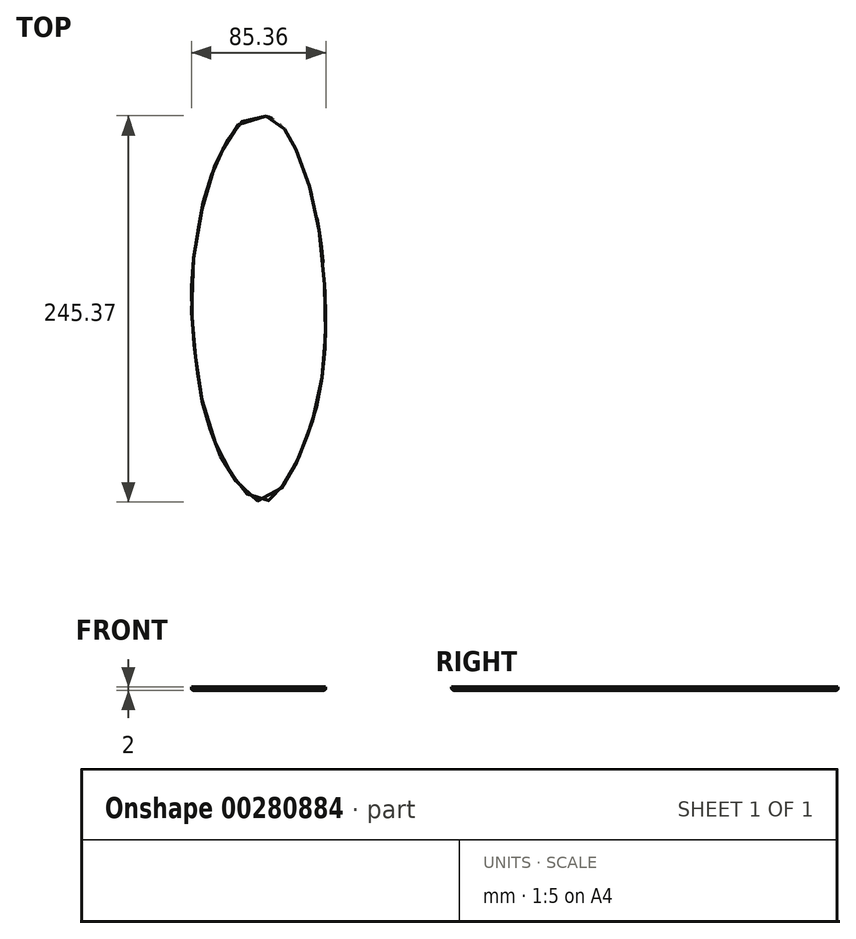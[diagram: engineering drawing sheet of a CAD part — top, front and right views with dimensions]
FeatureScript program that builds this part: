
annotation { "Feature Type Name" : "Feature", "Feature Type Description" : "" }
export const myFeature = defineFeature(function(context is Context, id is Id, definition is map)
    precondition{}
    {
        {
            var Q0;
            Q0=qCreatedBy(makeId("Top.planeOp"),FACE);
            var sketch = newSketch(context, id + "F0", { "sketchPlane" : qUnion([Q0])});
            skPoint(sketch, "E0", {"position": v(0, 122.5) * mm});
            skLineSegment(sketch, "E1", {"start": v(0, 122.5) * mm, "end": v(0, 120) * mm, "construction": true});
            skLineSegment(sketch, "E2", {"start": v(0, 120) * mm, "end": v(0, 117.5) * mm, "construction": true});
            skLineSegment(sketch, "E3", {"start": v(0, 117.5) * mm, "end": v(0, 112.5) * mm, "construction": true});
            skLineSegment(sketch, "E4", {"start": v(0, 112.5) * mm, "end": v(0, 107.5) * mm, "construction": true});
            skLineSegment(sketch, "E5", {"start": v(0, 107.5) * mm, "end": v(0, 102.5) * mm, "construction": true});
            skLineSegment(sketch, "E6", {"start": v(0, 102.5) * mm, "end": v(0, 92.5) * mm, "construction": true});
            skLineSegment(sketch, "E7", {"start": v(0, 92.5) * mm, "end": v(0, 72.5) * mm, "construction": true});
            skLineSegment(sketch, "E8", {"start": v(0, 72.5) * mm, "end": v(0, 52.5) * mm, "construction": true});
            skLineSegment(sketch, "E9", {"start": v(0, 52.5) * mm, "end": v(0, 22.5) * mm, "construction": true});
            skLineSegment(sketch, "E10", {"start": v(0, 22.5) * mm, "end": v(0, -7.5) * mm, "construction": true});
            skLineSegment(sketch, "E11", {"start": v(0, -7.5) * mm, "end": v(0, -27.5) * mm, "construction": true});
            skLineSegment(sketch, "E12", {"start": v(0, -27.5) * mm, "end": v(0, -47.5) * mm, "construction": true});
            skLineSegment(sketch, "E13", {"start": v(0, -47.5) * mm, "end": v(0, -67.5) * mm, "construction": true});
            skLineSegment(sketch, "E14", {"start": v(0, -67.5) * mm, "end": v(0, -87.5) * mm, "construction": true});
            skLineSegment(sketch, "E15", {"start": v(0, -87.5) * mm, "end": v(0, -97.5) * mm, "construction": true});
            skLineSegment(sketch, "E16", {"start": v(0, -97.5) * mm, "end": v(0, -107.5) * mm, "construction": true});
            skLineSegment(sketch, "E17", {"start": v(0, -107.5) * mm, "end": v(0, -112.5) * mm, "construction": true});
            skLineSegment(sketch, "E18", {"start": v(0, -112.5) * mm, "end": v(0, -117.5) * mm, "construction": true});
            skLineSegment(sketch, "E19", {"start": v(0, -117.5) * mm, "end": v(0, -120) * mm, "construction": true});
            skLineSegment(sketch, "E20", {"start": v(0, -120) * mm, "end": v(0, -122.5) * mm, "construction": true});
            skLineSegment(sketch, "E21", {"start": v(0, -7.5) * mm, "end": v(40, -7.5) * mm, "construction": true});
            skLineSegment(sketch, "E22", {"start": v(0, -7.5) * mm, "end": v(-44.8, -7.5) * mm, "construction": true});
            skLineSegment(sketch, "E23", {"start": v(0, 120) * mm, "end": v(8.2, 120) * mm, "construction": true});
            skLineSegment(sketch, "E24", {"start": v(0, 117.5) * mm, "end": v(11.3, 117.5) * mm, "construction": true});
            skLineSegment(sketch, "E25", {"start": v(0, 112.5) * mm, "end": v(15, 112.5) * mm, "construction": true});
            skLineSegment(sketch, "E26", {"start": v(0, 107.5) * mm, "end": v(18.1, 107.5) * mm, "construction": true});
            skLineSegment(sketch, "E27", {"start": v(0, 102.5) * mm, "end": v(20.5, 102.5) * mm, "construction": true});
            skLineSegment(sketch, "E28", {"start": v(0, 92.5) * mm, "end": v(24.7, 92.5) * mm, "construction": true});
            skLineSegment(sketch, "E29", {"start": v(0, 72.5) * mm, "end": v(31.1, 72.5) * mm, "construction": true});
            skLineSegment(sketch, "E30", {"start": v(0, 52.5) * mm, "end": v(35.4, 52.5) * mm, "construction": true});
            skLineSegment(sketch, "E31", {"start": v(0, 22.5) * mm, "end": v(38.9, 22.5) * mm, "construction": true});
            skLineSegment(sketch, "E32", {"start": v(0, 120) * mm, "end": v(-11.3, 120) * mm, "construction": true});
            skLineSegment(sketch, "E33", {"start": v(0, 117.5) * mm, "end": v(-15.2, 117.5) * mm, "construction": true});
            skLineSegment(sketch, "E34", {"start": v(0, 112.5) * mm, "end": v(-19.1, 112.5) * mm, "construction": true});
            skLineSegment(sketch, "E35", {"start": v(0, 107.5) * mm, "end": v(-22.4, 107.5) * mm, "construction": true});
            skLineSegment(sketch, "E36", {"start": v(0, 102.5) * mm, "end": v(-24.9, 102.5) * mm, "construction": true});
            skLineSegment(sketch, "E37", {"start": v(0, 92.5) * mm, "end": v(-29.8, 92.5) * mm, "construction": true});
            skLineSegment(sketch, "E38", {"start": v(0, 72.5) * mm, "end": v(-36.6, 72.5) * mm, "construction": true});
            skLineSegment(sketch, "E39", {"start": v(0, 52.5) * mm, "end": v(-40.7, 52.5) * mm, "construction": true});
            skLineSegment(sketch, "E40", {"start": v(0, 22.5) * mm, "end": v(-44.9, 22.5) * mm, "construction": true});
            skLineSegment(sketch, "E41", {"start": v(0, -27.5) * mm, "end": v(-43.1, -27.5) * mm, "construction": true});
            skLineSegment(sketch, "E42", {"start": v(0, -47.5) * mm, "end": v(-40.4, -47.5) * mm, "construction": true});
            skLineSegment(sketch, "E43", {"start": v(0, -67.5) * mm, "end": v(-36.2, -67.5) * mm, "construction": true});
            skLineSegment(sketch, "E44", {"start": v(0, -87.5) * mm, "end": v(-29.1, -87.5) * mm, "construction": true});
            skLineSegment(sketch, "E45", {"start": v(0, -97.5) * mm, "end": v(-24.6, -97.5) * mm, "construction": true});
            skLineSegment(sketch, "E46", {"start": v(0, -107.5) * mm, "end": v(-18.1, -107.5) * mm, "construction": true});
            skLineSegment(sketch, "E47", {"start": v(0, -112.5) * mm, "end": v(-14.4, -112.5) * mm, "construction": true});
            skLineSegment(sketch, "E48", {"start": v(0, -27.5) * mm, "end": v(39.5, -27.5) * mm, "construction": true});
            skLineSegment(sketch, "E49", {"start": v(0, -47.5) * mm, "end": v(37, -47.5) * mm, "construction": true});
            skLineSegment(sketch, "E50", {"start": v(0, -67.5) * mm, "end": v(32.5, -67.5) * mm, "construction": true});
            skLineSegment(sketch, "E51", {"start": v(0, -87.5) * mm, "end": v(25.6, -87.5) * mm, "construction": true});
            skLineSegment(sketch, "E52", {"start": v(0, -97.5) * mm, "end": v(21.2, -97.5) * mm, "construction": true});
            skLineSegment(sketch, "E53", {"start": v(0, -107.5) * mm, "end": v(15.7, -107.5) * mm, "construction": true});
            skLineSegment(sketch, "E54", {"start": v(0, -112.5) * mm, "end": v(12.7, -112.5) * mm, "construction": true});
            skLineSegment(sketch, "E55", {"start": v(0, -117.5) * mm, "end": v(9, -117.5) * mm, "construction": true});
            skLineSegment(sketch, "E56", {"start": v(0, -120) * mm, "end": v(6.5, -120) * mm, "construction": true});
            skLineSegment(sketch, "E57", {"start": v(0, -117.5) * mm, "end": v(-9.6, -117.5) * mm, "construction": true});
            skLineSegment(sketch, "E58", {"start": v(0, -120) * mm, "end": v(-6.4, -120) * mm, "construction": true});
            skLineSegment(sketch, "E59", {"start": v(0, 122.5) * mm, "end": v(2, 122.5) * mm});
            skLineSegment(sketch, "E60", {"start": v(0, 122.5) * mm, "end": v(-4.5, 122.5) * mm, "construction": true});
            skFitSpline(sketch, "E61", {"points": [v(40, -7.5) * mm, v(38.9, 22.5) * mm, v(35.4, 52.5) * mm, v(31.1, 72.5) * mm, v(24.7, 92.5) * mm, v(20.5, 102.5) * mm, v(18.1, 107.5) * mm, v(15, 112.5) * mm, v(11.3, 117.5) * mm, v(8.2, 120) * mm, v(2, 122.5) * mm, v(-4.5, 122.5) * mm, v(-11.3, 120) * mm, v(-15.2, 117.5) * mm, v(-19.1, 112.5) * mm, v(-22.4, 107.5) * mm, v(-24.9, 102.5) * mm, v(-29.8, 92.5) * mm, v(-36.6, 72.5) * mm, v(-40.7, 52.5) * mm, v(-44.9, 22.5) * mm, v(-44.8, -7.5) * mm, v(-43.1, -27.5) * mm, v(-40.4, -47.5) * mm, v(-36.2, -67.5) * mm, v(-29.1, -87.5) * mm, v(-24.6, -97.5) * mm, v(-18.1, -107.5) * mm, v(-14.4, -112.5) * mm, v(-9.6, -117.5) * mm, v(-6.4, -120) * mm, v(0, -122.5) * mm, v(6.5, -120) * mm, v(9, -117.5) * mm, v(12.7, -112.5) * mm, v(15.7, -107.5) * mm, v(21.2, -97.5) * mm, v(25.6, -87.5) * mm, v(32.5, -67.5) * mm, v(37, -47.5) * mm, v(39.5, -27.5) * mm, v(40, -7.5) * mm]});
            skSolve(sketch);
        }
        {
            var Q0;
            Q0 = qSketchRegion(id + "F0", true);
            extrude(context, id + "F1", {"entities" : qUnion([Q0]), "depth" : 2 * mm});
        }
        {
            var Q0;
            Q0=makeQuery(id+"F1.opExtrude","CAP_EDGE",EDGE,{"disambiguationData":[OSD([sQuery(id+"F0.wireOp",EDGE,"E61")])],"isStart":true});
            fillet(context, id + "F2", {"entities" : qUnion([Q0]), "radius" : 1.27 * mm, "tangentPropagation" : true, "allowEdgeOverflow" : false});
        }
        {
            var Q0;
            Q0=qCreatedBy(makeId("Right.planeOp"),FACE);
            cPlane(context, id + "F3", {"entities" : qUnion([Q0]), "cplaneType" : CPlaneType.OFFSET, "offset" : 75 * mm, "width" : 150 * mm, "height" : 150 * mm});
        }
    });
